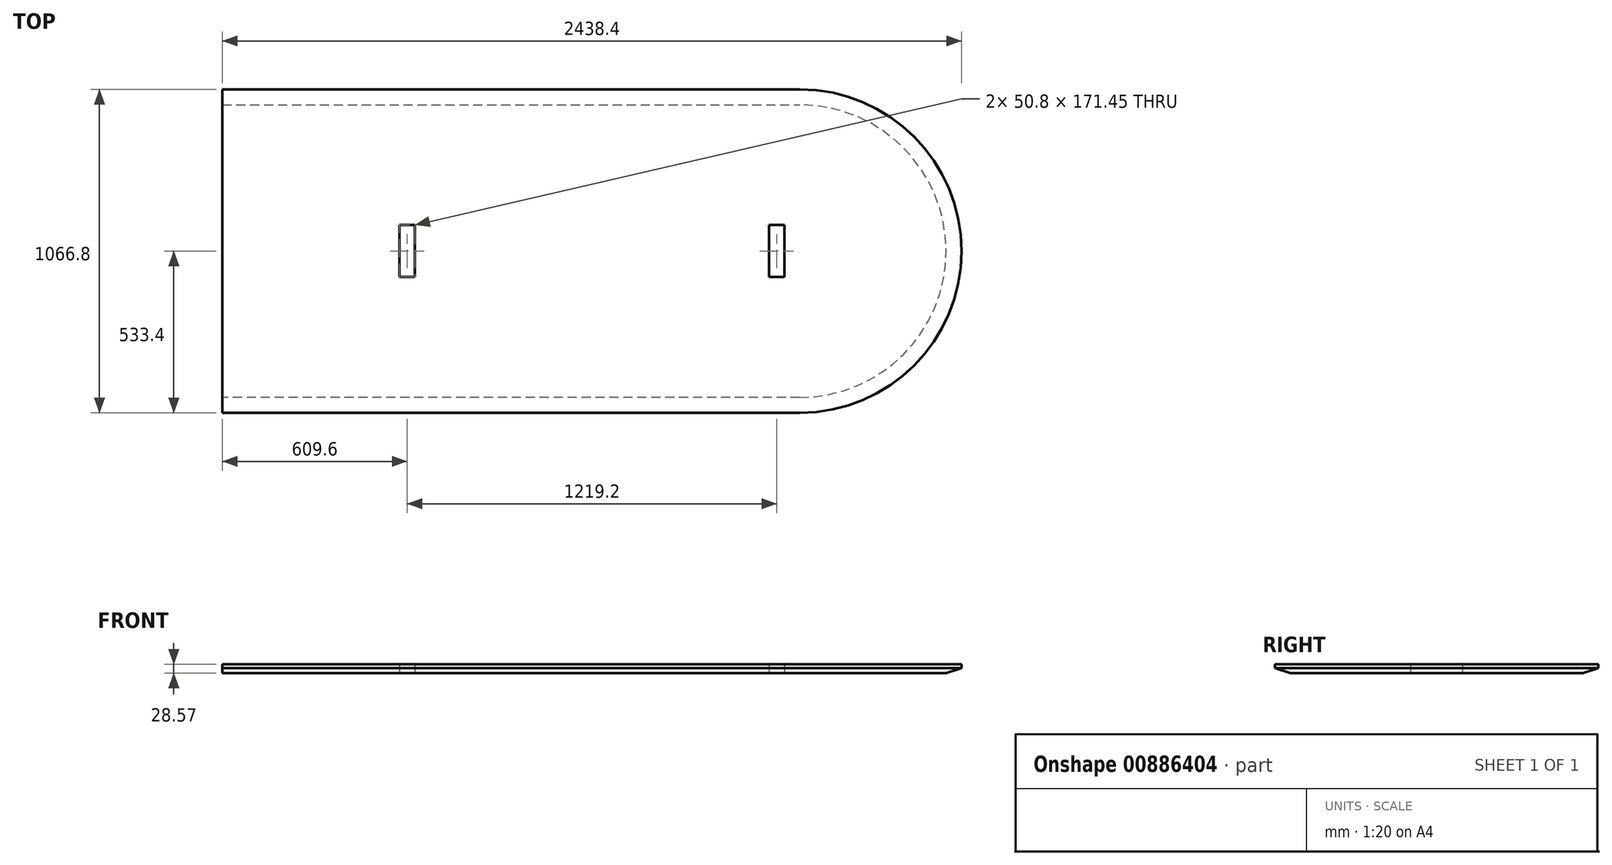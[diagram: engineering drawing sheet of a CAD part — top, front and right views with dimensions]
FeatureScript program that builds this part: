
annotation { "Feature Type Name" : "Feature", "Feature Type Description" : "" }
export const myFeature = defineFeature(function(context is Context, id is Id, definition is map)
    precondition{}
    {
        {
            var Q0;
            Q0=qCreatedBy(makeId("Top.planeOp"),FACE);
            var sketch = newSketch(context, id + "F0", { "sketchPlane" : qUnion([Q0])});
            skLineSegment(sketch, "E0.bottom", {"start": v(1219.2, 533.4) * mm, "end": v(-1219.2, 533.4) * mm});
            skLineSegment(sketch, "E0.top", {"start": v(1219.2, -533.4) * mm, "end": v(-1219.2, -533.4) * mm});
            skLineSegment(sketch, "E0.left", {"start": v(1219.2, 533.4) * mm, "end": v(1219.2, -533.4) * mm});
            skLineSegment(sketch, "E0.right", {"start": v(-1219.2, 533.4) * mm, "end": v(-1219.2, -533.4) * mm});
            skPoint(sketch, "E0.middle", {"position": v(0, 0) * mm});
            skLineSegment(sketch, "E1", {"start": v(1219.2, 0) * mm, "end": v(685.8, 0) * mm});
            skArc(sketch, "E2", {"start": v(685.8, 533.4) * mm, "mid": v(1219.2, 0) * mm, "end": v(685.8, -533.4) * mm});
            skLineSegment(sketch, "E3", {"start": v(0, 0) * mm, "end": v(609.6, 0) * mm});
            skLineSegment(sketch, "E4", {"start": v(0, 0) * mm, "end": v(-609.6, 0) * mm});
            skLineSegment(sketch, "E5.bottom", {"start": v(-584.2, 85.72) * mm, "end": v(-635, 85.72) * mm});
            skLineSegment(sketch, "E5.top", {"start": v(-584.2, -85.73) * mm, "end": v(-635, -85.73) * mm});
            skLineSegment(sketch, "E5.left", {"start": v(-584.2, 85.72) * mm, "end": v(-584.2, -85.73) * mm});
            skLineSegment(sketch, "E5.right", {"start": v(-635, 85.72) * mm, "end": v(-635, -85.73) * mm});
            skPoint(sketch, "E5.middle", {"position": v(-609.6, 0) * mm});
            skLineSegment(sketch, "E6.bottom", {"start": v(635, 85.73) * mm, "end": v(584.2, 85.73) * mm});
            skLineSegment(sketch, "E6.top", {"start": v(635, -85.72) * mm, "end": v(584.2, -85.72) * mm});
            skLineSegment(sketch, "E6.left", {"start": v(635, 85.73) * mm, "end": v(635, -85.73) * mm});
            skLineSegment(sketch, "E6.right", {"start": v(584.2, 85.73) * mm, "end": v(584.2, -85.73) * mm});
            skPoint(sketch, "E6.middle", {"position": v(609.6, 0) * mm});
            skSolve(sketch);
        }
        {
            var Q0;
            {var subQ4=sQuery(id+"F0.wireOp",EDGE,"E0.right");Q0=makeQuery(id+"F0.imprint","IMPRINT",FACE,{"disambiguationData":[TD([[makeQuery(id+"F0.imprint","IMPRINT",EDGE,{"derivedFrom":subQ4}),1.0]])]});}
            extrude(context, id + "F1", {"entities" : qUnion([Q0]), "depth" : 28.57 * mm, "offsetDistance" : 25.4 * mm});
        }
        {
            var Q0;
            Q0=makeQuery(id+"F1.opExtrude","CAP_EDGE",EDGE,{"disambiguationData":[OSD([sQuery(id+"F0.wireOp",EDGE,"E0.top")])],"isStart":true});
            var Q1;
            Q1=makeQuery(id+"F1.opExtrude","CAP_EDGE",EDGE,{"disambiguationData":[OSD([sQuery(id+"F0.wireOp",EDGE,"E2")])],"isStart":true});
            var Q2;
            Q2=makeQuery(id+"F1.opExtrude","CAP_EDGE",EDGE,{"disambiguationData":[OSD([sQuery(id+"F0.wireOp",EDGE,"E0.bottom")])],"isStart":true});
            chamfer(context, id + "F2", {"entities" : qUnion([Q0, Q1, Q2]), "chamferType" : ChamferType.TWO_OFFSETS, "width1" : 50.8 * mm, "oppositeDirection" : false, "width2" : 15.88 * mm, "tangentPropagation" : true});
        }
    });
